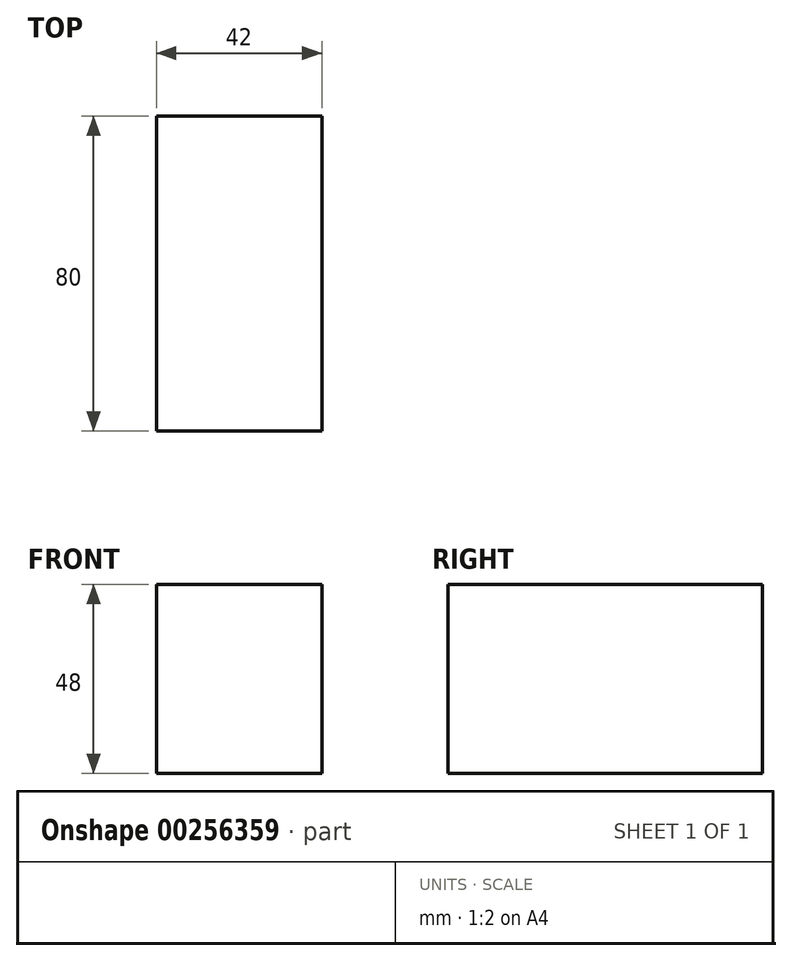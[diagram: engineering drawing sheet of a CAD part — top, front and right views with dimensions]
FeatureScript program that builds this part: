
annotation { "Feature Type Name" : "Feature", "Feature Type Description" : "" }
export const myFeature = defineFeature(function(context is Context, id is Id, definition is map)
    precondition{}
    {
        {
            var Q0;
            Q0=qCreatedBy(makeId("Top.planeOp"),FACE);
            var sketch = newSketch(context, id + "F0", { "sketchPlane" : qUnion([Q0])});
            skLineSegment(sketch, "E0.bottom", {"start": v(0, 0) * mm, "end": v(42, 0) * mm});
            skLineSegment(sketch, "E0.top", {"start": v(0, 80) * mm, "end": v(42, 80) * mm});
            skLineSegment(sketch, "E0.left", {"start": v(0, 0) * mm, "end": v(0, 80) * mm});
            skLineSegment(sketch, "E0.right", {"start": v(42, 0) * mm, "end": v(42, 80) * mm});
            skSolve(sketch);
        }
        {
            var Q0;
            Q0=makeQuery(id+"F0.imprint","IMPRINT",FACE,{"disambiguationData":[TD([[makeQuery(id+"F0.imprint","IMPRINT",EDGE,{"derivedFrom":sQuery(id+"F0.wireOp",EDGE,"E0.bottom")}),1.0]])]});
            extrude(context, id + "F1", {"entities" : qUnion([Q0]), "depth" : 48 * mm});
        }
    });
